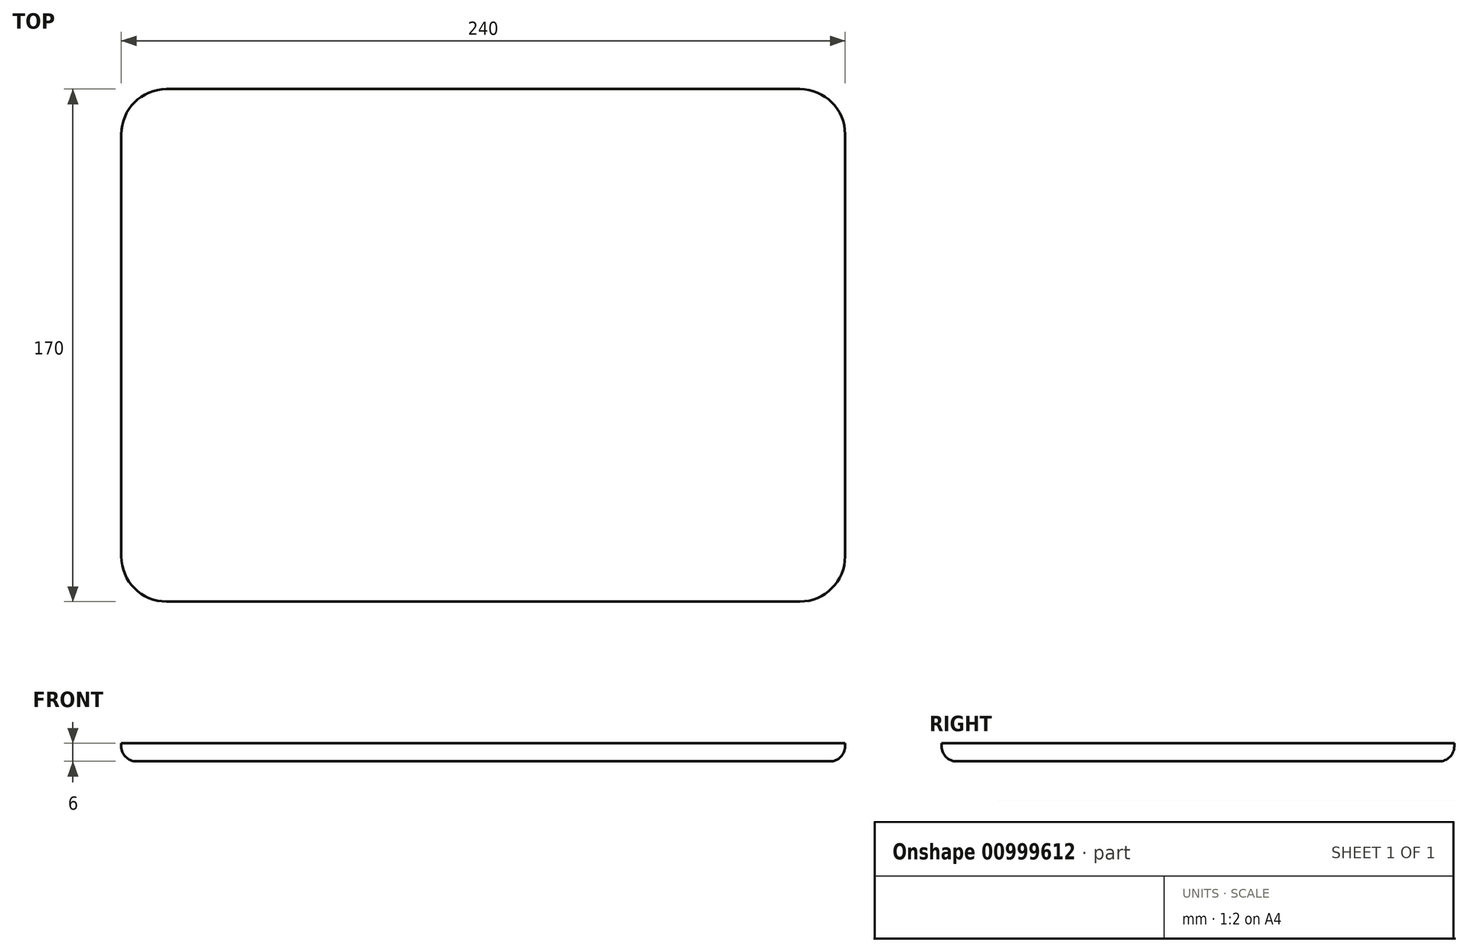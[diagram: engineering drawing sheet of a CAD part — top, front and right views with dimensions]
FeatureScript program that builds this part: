
annotation { "Feature Type Name" : "Feature", "Feature Type Description" : "" }
export const myFeature = defineFeature(function(context is Context, id is Id, definition is map)
    precondition{}
    {
        {
            var Q0;
            Q0=qCreatedBy(makeId("Top.planeOp"),FACE);
            var sketch = newSketch(context, id + "F0", { "sketchPlane" : qUnion([Q0])});
            skLineSegment(sketch, "E0.bottom", {"start": v(120, 85) * mm, "end": v(-120, 85) * mm});
            skLineSegment(sketch, "E0.top", {"start": v(120, -85) * mm, "end": v(-120, -85) * mm});
            skLineSegment(sketch, "E0.left", {"start": v(120, 85) * mm, "end": v(120, -85) * mm});
            skLineSegment(sketch, "E0.right", {"start": v(-120, 85) * mm, "end": v(-120, -85) * mm});
            skPoint(sketch, "E0.middle", {"position": v(0, 0) * mm});
            skSolve(sketch);
        }
        {
            var Q0;
            Q0=makeQuery(id+"F0.imprint","IMPRINT",FACE,{"disambiguationData":[TD([[makeQuery(id+"F0.imprint","IMPRINT",EDGE,{"derivedFrom":sQuery(id+"F0.wireOp",EDGE,"E0.bottom")}),1.0]])]});
            extrude(context, id + "F1", {"entities" : qUnion([Q0]), "depth" : 6 * mm, "offsetDistance" : 25 * mm});
        }
        {
            var Q0;
            Q0=makeQuery(id+"F1.opExtrude","SWEPT_EDGE",EDGE,{"disambiguationData":[OSD([sQuery(id+"F0.wireOp",EDGE,"E0.top"),sQuery(id+"F0.wireOp",EDGE,"E0.right")])]});
            var Q1;
            Q1=makeQuery(id+"F1.opExtrude","SWEPT_EDGE",EDGE,{"disambiguationData":[OSD([sQuery(id+"F0.wireOp",EDGE,"E0.bottom"),sQuery(id+"F0.wireOp",EDGE,"E0.right")])]});
            var Q2;
            Q2=makeQuery(id+"F1.opExtrude","SWEPT_EDGE",EDGE,{"disambiguationData":[OSD([sQuery(id+"F0.wireOp",EDGE,"E0.bottom"),sQuery(id+"F0.wireOp",EDGE,"E0.left")])]});
            var Q3;
            Q3=makeQuery(id+"F1.opExtrude","SWEPT_EDGE",EDGE,{"disambiguationData":[OSD([sQuery(id+"F0.wireOp",EDGE,"E0.top"),sQuery(id+"F0.wireOp",EDGE,"E0.left")])]});
            fillet(context, id + "F2", {"entities" : qUnion([Q0, Q1, Q2, Q3]), "radius" : 15 * mm, "tangentPropagation" : true, "allowEdgeOverflow" : false});
        }
        {
            var Q0;
            Q0=makeQuery(id+"F1.opExtrude","CAP_FACE",FACE,{"disambiguationData":[OSD([sQuery(id+"F0.wireOp",EDGE,"E0.bottom"),sQuery(id+"F0.wireOp",EDGE,"E0.top"),sQuery(id+"F0.wireOp",EDGE,"E0.left"),sQuery(id+"F0.wireOp",EDGE,"E0.right")])],"isStart":true});
            fillet(context, id + "F3", {"entities" : qUnion([Q0]), "radius" : 5 * mm, "tangentPropagation" : true, "allowEdgeOverflow" : false});
        }
    });
